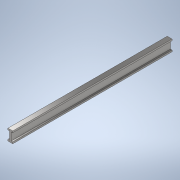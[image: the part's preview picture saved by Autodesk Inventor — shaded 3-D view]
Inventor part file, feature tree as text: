
AUTODESK INVENTOR PART (.ipt)
format: ipt  version: 2021 (Build 250183000, 183)  size: 108,032 bytes
history: native  units: in
note: dims shown in document units (in); Inventor stores cm internally (conversion verified against a paired STEP export)
features: extrude x1, sketch x1
ambient origin geometry x8: Origin, YZ Plane, XZ Plane, XY Plane, X Axis, Y Axis, Z Axis, Center Point
bodies: Solid1 (feature_tree)
feature tree (2):
  extrude  "Extrusion1"  Depth=0.7874in
  sketch  "Sketch1"  dims[d4=1.9685in d5=0.7874in d6=0.7874in d7=78.7402in d8=0.0in]
